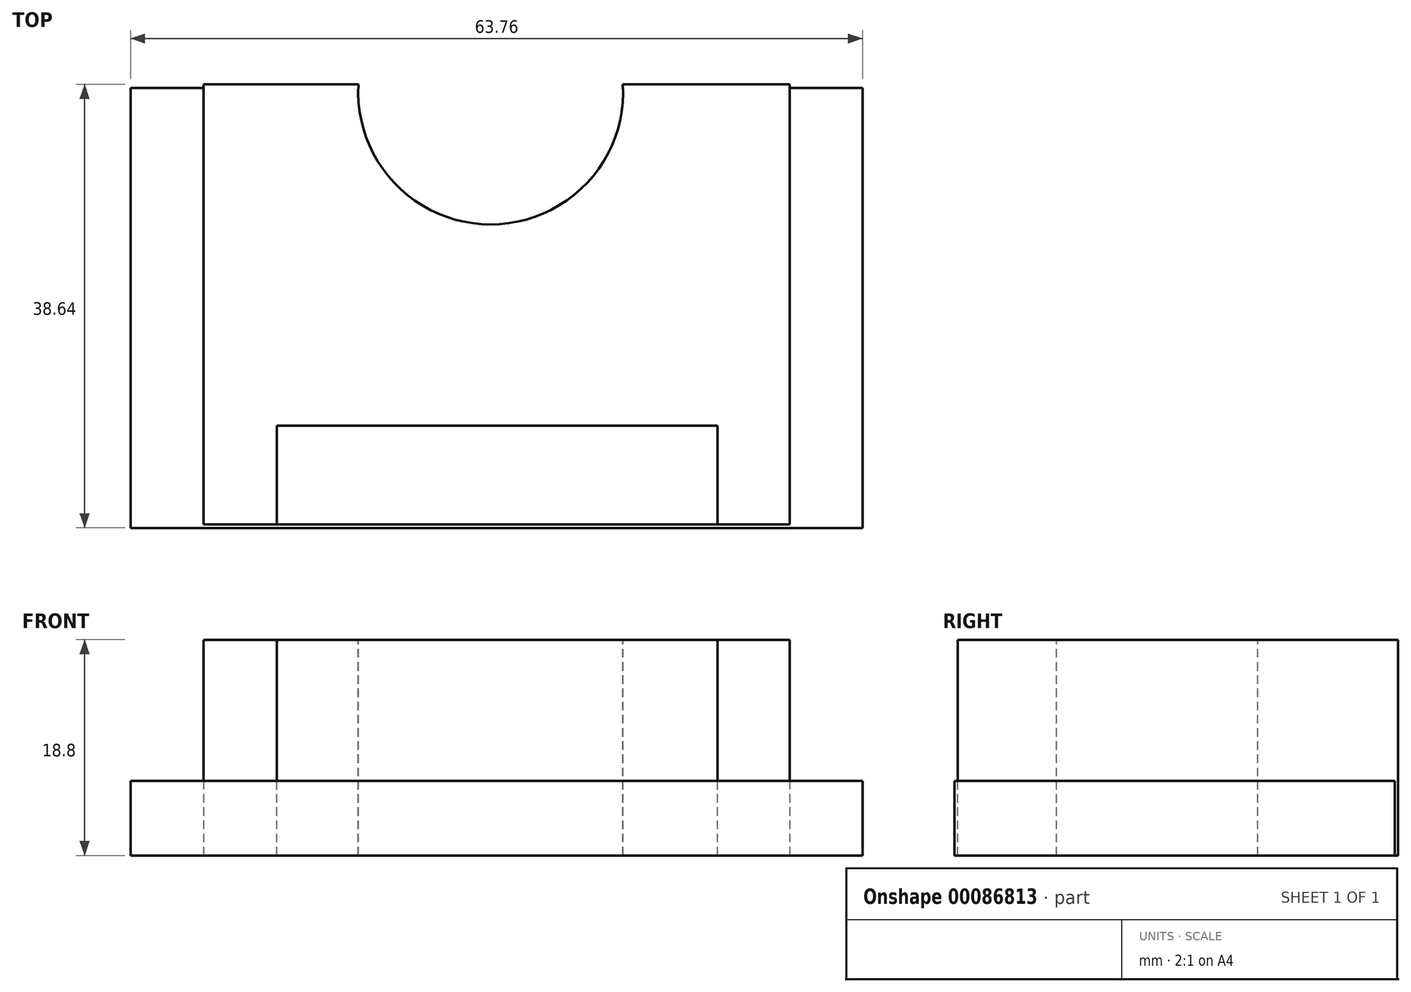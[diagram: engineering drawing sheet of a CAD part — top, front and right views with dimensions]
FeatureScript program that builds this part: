
annotation { "Feature Type Name" : "Feature", "Feature Type Description" : "" }
export const myFeature = defineFeature(function(context is Context, id is Id, definition is map)
    precondition{}
    {
        {
            var Q0;
            Q0=qCreatedBy(makeId("Top.planeOp"),FACE);
            var sketch = newSketch(context, id + "F0", { "sketchPlane" : qUnion([Q0])});
            skLineSegment(sketch, "E0.bottom", {"start": v(-31.88, 19.13) * mm, "end": v(31.88, 19.13) * mm});
            skLineSegment(sketch, "E0.top", {"start": v(-31.88, -19.22) * mm, "end": v(31.88, -19.22) * mm});
            skLineSegment(sketch, "E0.left", {"start": v(-31.88, 19.13) * mm, "end": v(-31.88, -19.22) * mm});
            skLineSegment(sketch, "E0.right", {"start": v(31.88, 19.13) * mm, "end": v(31.88, -19.22) * mm});
            skLineSegment(sketch, "E1", {"start": v(0, 48.39) * mm, "end": v(0, -43.62) * mm, "construction": true});
            skLineSegment(sketch, "E2", {"start": v(-43.73, -0.05) * mm, "end": v(64.37, -0.05) * mm, "construction": true});
            skPoint(sketch, "E2.startSnap0", {"position": v(-31.88, -0.05) * mm});
            skSolve(sketch);
        }
        {
            var Q0;
            Q0=makeQuery(id+"F0.imprint","IMPRINT",FACE,{"disambiguationData":[TD([[makeQuery(id+"F0.imprint","IMPRINT",EDGE,{"derivedFrom":sQuery(id+"F0.wireOp",EDGE,"E0.bottom")}),-1.0]])]});
            extrude(context, id + "F1", {"entities" : qUnion([Q0]), "depth" : 6.5 * mm});
        }
        {
            var Q0;
            Q0=qCreatedBy(makeId("Top.planeOp"),FACE);
            var sketch = newSketch(context, id + "F2", { "sketchPlane" : qUnion([Q0])});
            skLineSegment(sketch, "E3.bottom", {"start": v(-25.53, 19.42) * mm, "end": v(25.53, 19.42) * mm});
            skLineSegment(sketch, "E3.top", {"start": v(-25.53, -18.93) * mm, "end": v(25.53, -18.93) * mm});
            skLineSegment(sketch, "E3.left", {"start": v(-25.53, 19.42) * mm, "end": v(-25.53, -18.93) * mm});
            skLineSegment(sketch, "E3.right", {"start": v(25.53, 19.42) * mm, "end": v(25.53, -18.93) * mm});
            skSolve(sketch);
        }
        {
            var Q0;
            Q0 = qSketchRegion(id + "F2", true);
            extrude(context, id + "F3", {"entities" : qUnion([Q0]), "operationType" : NewBodyOperationType.ADD, "depth" : 18.8 * mm});
        }
        {
            var Q0;
            Q0=makeQuery(id+"F3.opExtrude","CAP_FACE",FACE,{"disambiguationData":[OSD([sQuery(id+"F2.wireOp",EDGE,"E3.bottom"),sQuery(id+"F2.wireOp",EDGE,"E3.top"),sQuery(id+"F2.wireOp",EDGE,"E3.left"),sQuery(id+"F2.wireOp",EDGE,"E3.right")])],"isStart":false});
            var sketch = newSketch(context, id + "F4", { "sketchPlane" : qUnion([Q0])});
            skLineSegment(sketch, "E4.bottom", {"start": v(-19.14, -10.32) * mm, "end": v(19.26, -10.32) * mm});
            skLineSegment(sketch, "E4.top", {"start": v(-19.14, -18.93) * mm, "end": v(19.26, -18.93) * mm});
            skLineSegment(sketch, "E4.left", {"start": v(-19.14, -10.32) * mm, "end": v(-19.14, -18.93) * mm});
            skLineSegment(sketch, "E4.right", {"start": v(19.26, -10.32) * mm, "end": v(19.26, -18.93) * mm});
            skSolve(sketch);
        }
        {
            var Q0;
            Q0=makeQuery(id+"F4.imprint","IMPRINT",FACE,{"disambiguationData":[TD([[makeQuery(id+"F4.imprint","IMPRINT",EDGE,{"derivedFrom":sQuery(id+"F4.wireOp",EDGE,"E4.bottom")}),-1.0]])]});
            extrude(context, id + "F5", {"entities" : qUnion([Q0]), "operationType" : NewBodyOperationType.REMOVE, "oppositeDirection" : true, "depth" : 25.4 * mm});
        }
        {
            var Q0;
            Q0=makeQuery(id+"F3.opExtrude","CAP_FACE",FACE,{"disambiguationData":[OSD([sQuery(id+"F2.wireOp",EDGE,"E3.bottom"),sQuery(id+"F2.wireOp",EDGE,"E3.top"),sQuery(id+"F2.wireOp",EDGE,"E3.left"),sQuery(id+"F2.wireOp",EDGE,"E3.right")])],"isStart":false});
            var sketch = newSketch(context, id + "F6", { "sketchPlane" : qUnion([Q0])});
            skArc(sketch, "E5", {"start": v(11.16, 19.42) * mm, "mid": v(-11.47, 22.84) * mm, "end": v(7.88, 10.61) * mm});
            skCircle(sketch, "E6", {"center": v(-0.51, 18.76) * mm, "radius": 11.54 * mm});
            skSolve(sketch);
        }
        {
            var Q0;
            {var subQ0=sQuery(id+"F6.wireOp",EDGE,"E6");var subQ1=makeQuery(id+"F3.opExtrude","CAP_EDGE",EDGE,{"disambiguationData":[OSD([sQuery(id+"F2.wireOp",EDGE,"E3.bottom")])],"isStart":false});var subQ2=makeQuery(id+"F6.imprint","INTERSECT",VERTEX,{"disambiguationData":[OD(0.0)],"derivedFrom":[subQ1,subQ0]});Q0=makeQuery(id+"F6.imprint","IMPRINT",FACE,{"disambiguationData":[TD([[makeQuery(id+"F6.imprint","IMPRINT",EDGE,{"disambiguationData":[TD([[subQ2,1.0]])],"derivedFrom":subQ0}),1.0]])]});}
            extrude(context, id + "F7", {"entities" : qUnion([Q0]), "operationType" : NewBodyOperationType.REMOVE, "endBound" : BoundingType.THROUGH_ALL, "oppositeDirection" : true, "depth" : 25.4 * mm});
        }
    });
